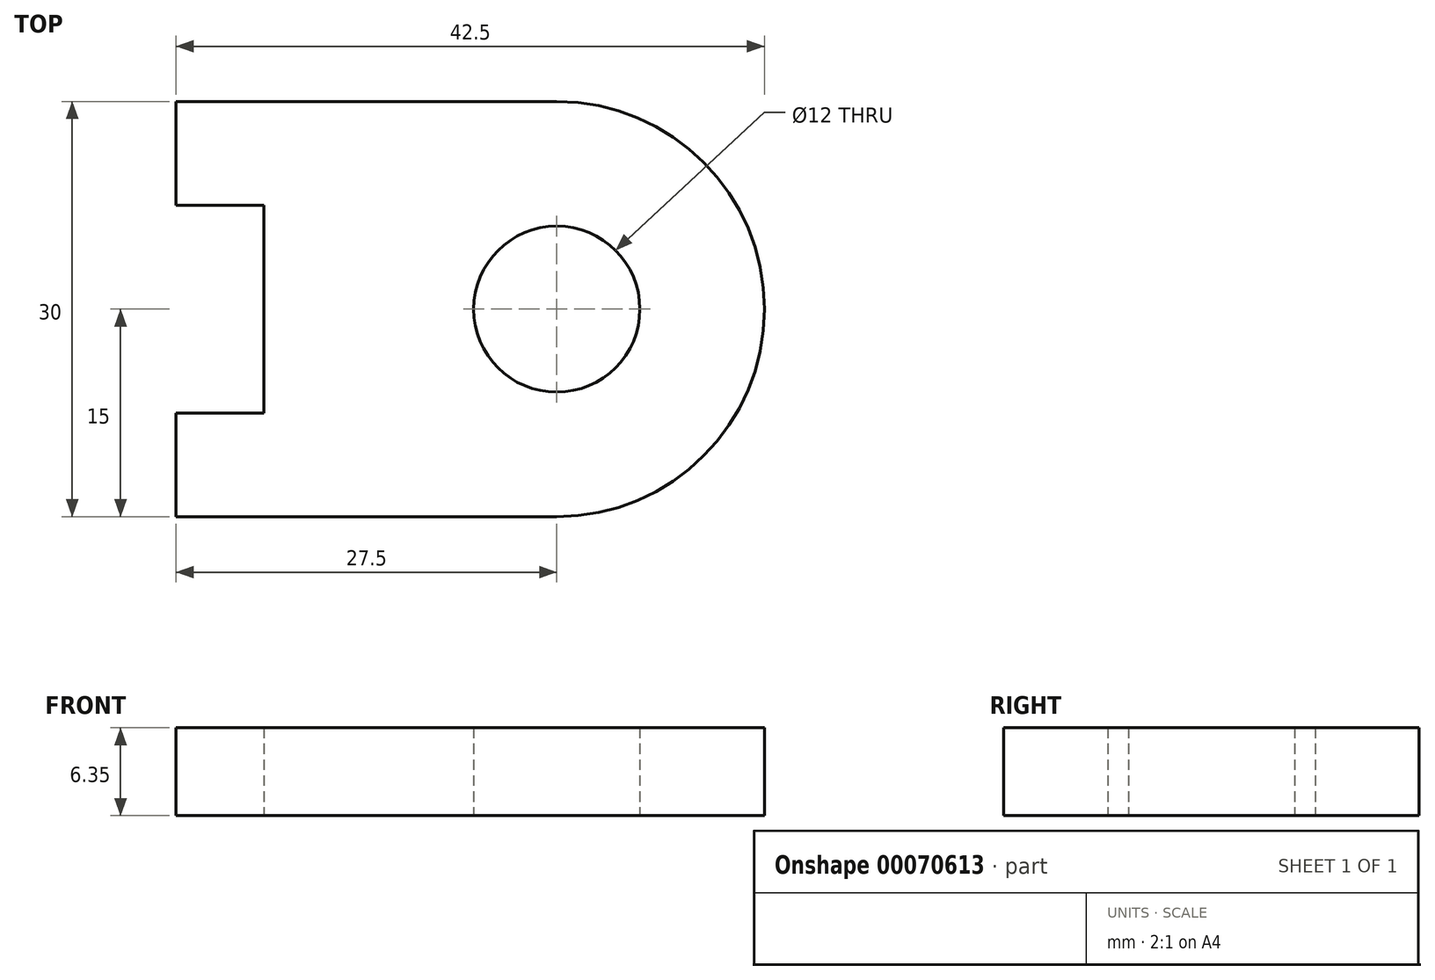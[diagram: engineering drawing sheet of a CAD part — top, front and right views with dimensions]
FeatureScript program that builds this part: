
annotation { "Feature Type Name" : "Feature", "Feature Type Description" : "" }
export const myFeature = defineFeature(function(context is Context, id is Id, definition is map)
    precondition{}
    {
        {
            var Q0;
            Q0=qCreatedBy(makeId("Top.planeOp"),FACE);
            var sketch = newSketch(context, id + "F0", { "sketchPlane" : qUnion([Q0])});
            skCircle(sketch, "E0", {"center": v(0, 0) * mm, "radius": 6 * mm});
            skLineSegment(sketch, "E1.bottom", {"start": v(-27.5, 7.5) * mm, "end": v(-21.15, 7.5) * mm});
            skLineSegment(sketch, "E1.top", {"start": v(-27.5, -7.5) * mm, "end": v(-21.15, -7.5) * mm});
            skLineSegment(sketch, "E1.left", {"start": v(-27.5, 7.5) * mm, "end": v(-27.5, -7.5) * mm});
            skLineSegment(sketch, "E1.right", {"start": v(-21.15, 7.5) * mm, "end": v(-21.15, -7.5) * mm});
            skLineSegment(sketch, "E2.bottom", {"start": v(-27.5, 15) * mm, "end": v(27.5, 15) * mm});
            skLineSegment(sketch, "E2.top", {"start": v(-27.5, -15) * mm, "end": v(27.5, -15) * mm});
            skLineSegment(sketch, "E2.left", {"start": v(-27.5, 15) * mm, "end": v(-27.5, -15) * mm});
            skLineSegment(sketch, "E2.right", {"start": v(27.5, 15) * mm, "end": v(27.5, -15) * mm});
            skCircle(sketch, "E3", {"center": v(0, 0) * mm, "radius": 15 * mm});
            skSolve(sketch);
        }
        {
            var Q0;
            Q0=makeQuery(id+"F0.imprint","IMPRINT",FACE,{"disambiguationData":[TD([[makeQuery(id+"F0.imprint","IMPRINT",EDGE,{"derivedFrom":sQuery(id+"F0.wireOp",EDGE,"hteyK1tT-BaRy-Fh7S-bQSy-bIsIVJuyDypa")}),1.0]])]});
            var Q1;
            Q1=makeQuery(id+"F0.imprint","IMPRINT",FACE,{"disambiguationData":[TD([[makeQuery(id+"F0.imprint","IMPRINT",EDGE,{"derivedFrom":sQuery(id+"F0.wireOp",EDGE,"E0")}),-1.0]])]});
            var Q2;
            {var subQ0=sQuery(id+"F0.wireOp",EDGE,"E2.bottom");Q2=makeQuery(id+"F0.imprint","IMPRINT",FACE,{"disambiguationData":[TD([[makeQuery(id+"F0.imprint","IMPRINT",EDGE,{"derivedFrom":subQ0}),1.0]])]});}
            var Q3;
            {var subQ0=sQuery(id+"F0.wireOp",EDGE,"7rRSdzhh-qalX-vf6y-f0YR-i6mPcpKjNE8b");var subQ1=sQuery(id+"F0.wireOp",EDGE,"E2.top");var subQ2=makeQuery(id+"F0.imprint","INTERSECT",VERTEX,{"disambiguationData":[OD(0.0)],"derivedFrom":[subQ1,subQ0]});Q3=makeQuery(id+"F0.imprint","IMPRINT",FACE,{"disambiguationData":[TD([[makeQuery(id+"F0.imprint","IMPRINT",EDGE,{"disambiguationData":[TD([[subQ2,-1.0]])],"derivedFrom":subQ1}),-1.0]])]});}
            var Q4;
            {var subQ8=sQuery(id+"F0.wireOp",EDGE,"E1.bottom");Q4=makeQuery(id+"F0.imprint","IMPRINT",FACE,{"disambiguationData":[TD([[makeQuery(id+"F0.imprint","IMPRINT",EDGE,{"derivedFrom":subQ8}),1.0]])]});}
            extrude(context, id + "F1", {"entities" : qUnion([Q0, Q1, Q2, Q3, Q4]), "depth" : 6.35 * mm});
        }
    });
